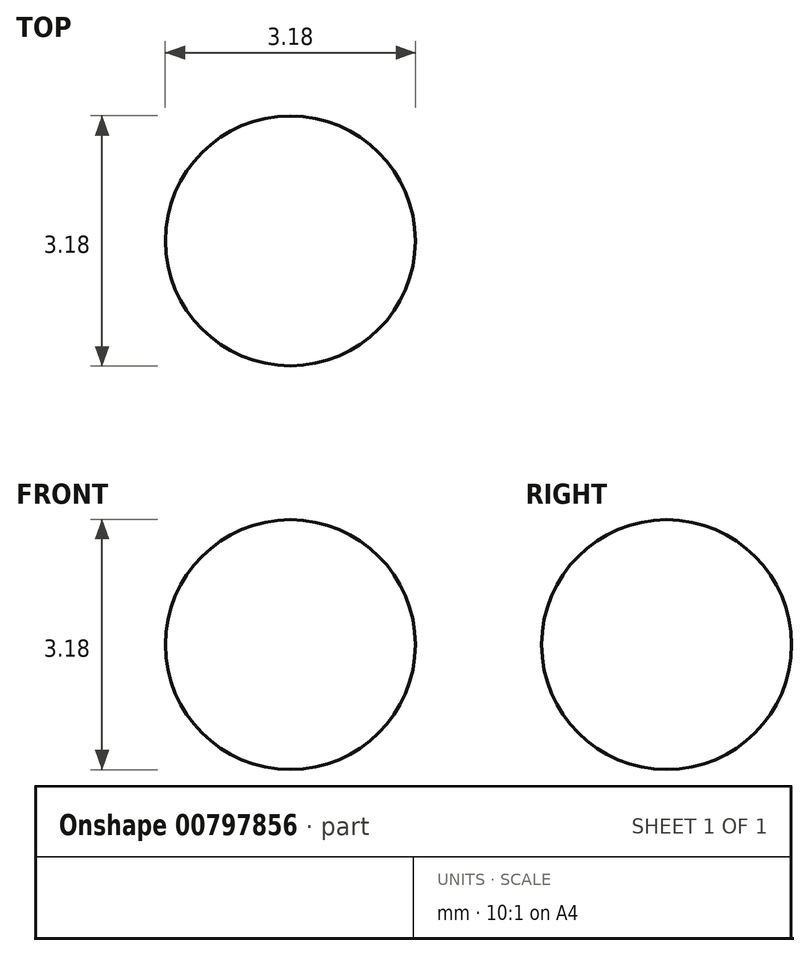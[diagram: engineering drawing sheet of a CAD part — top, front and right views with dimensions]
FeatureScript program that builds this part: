
annotation { "Feature Type Name" : "Feature", "Feature Type Description" : "" }
export const myFeature = defineFeature(function(context is Context, id is Id, definition is map)
    precondition{}
    {
        {
            var Q0;
            Q0=qCreatedBy(makeId("Front.planeOp"),FACE);
            var sketch = newSketch(context, id + "F0", { "sketchPlane" : qUnion([Q0])});
            skCircle(sketch, "E0", {"center": v(0, 0) * mm, "radius": 1.59 * mm});
            skLineSegment(sketch, "E1", {"start": v(0, 1.59) * mm, "end": v(0, 0) * mm});
            skLineSegment(sketch, "E2", {"start": v(0, 0) * mm, "end": v(0, -1.59) * mm});
            skSolve(sketch);
        }
        {
            var Q0;
            {var subQ0=sQuery(id+"F0.wireOp",EDGE,"E1");Q0=makeQuery(id+"F0.imprint","IMPRINT",FACE,{"disambiguationData":[TD([[makeQuery(id+"F0.imprint","IMPRINT",EDGE,{"derivedFrom":subQ0}),1.0]])]});}
            var Q1;
            Q1=sQuery(id+"F0.wireOp",EDGE,"E2");
            revolve(context, id + "F1", {"surfaceOperationType" : NewSurfaceOperationType.NEW, "entities" : qUnion([Q0]), "axis" : qUnion([Q1]), "revolveType" : RevolveType.FULL});
        }
    });
